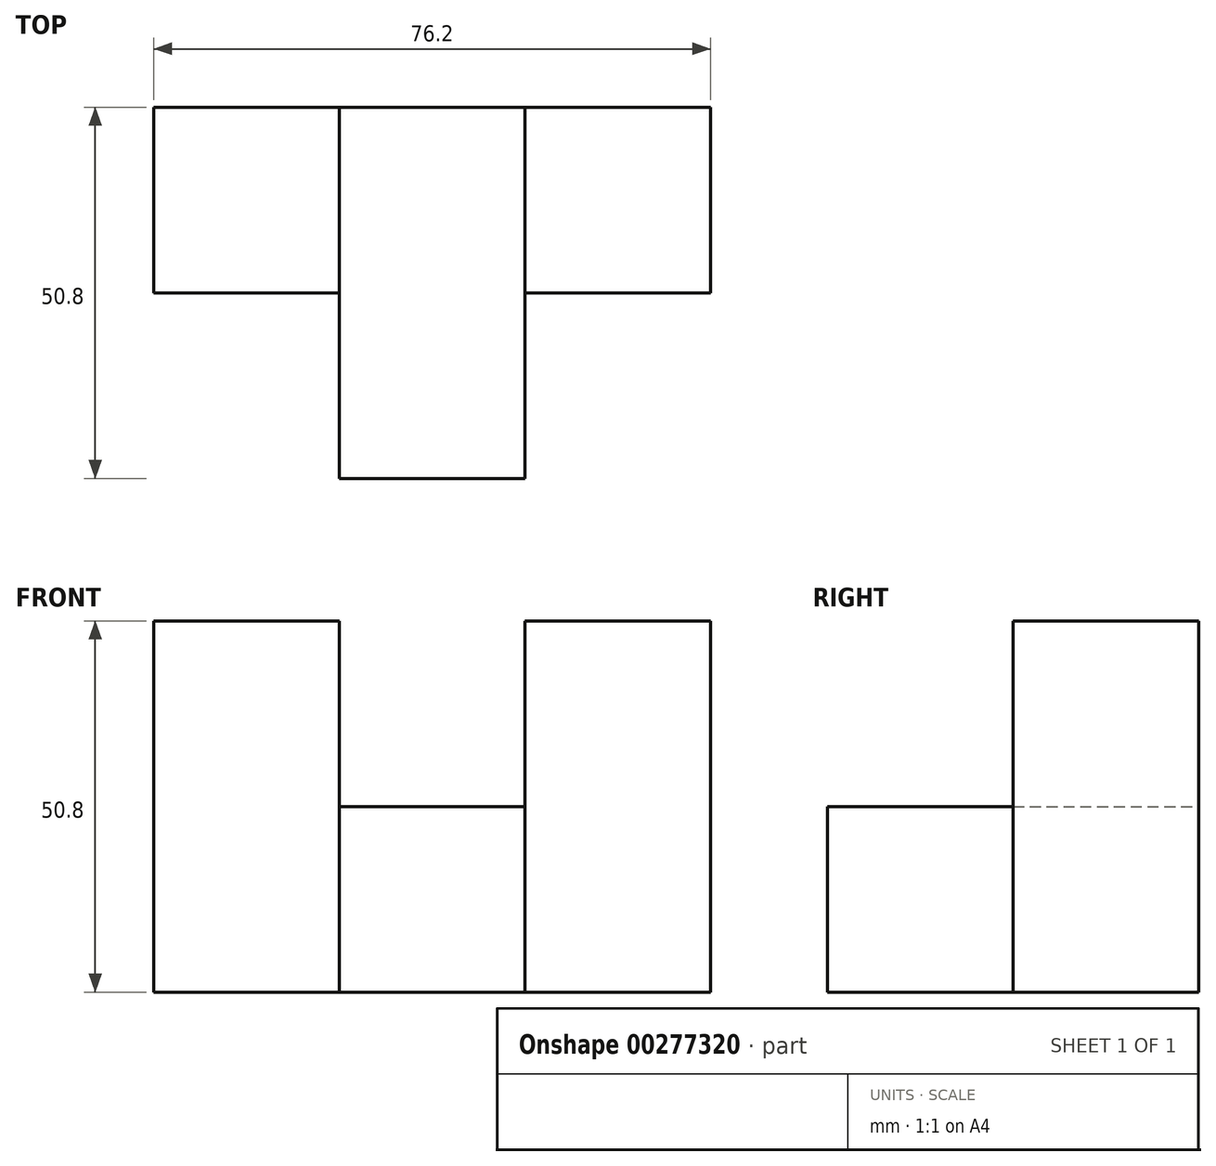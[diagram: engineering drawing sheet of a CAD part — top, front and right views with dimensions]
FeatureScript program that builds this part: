
annotation { "Feature Type Name" : "Feature", "Feature Type Description" : "" }
export const myFeature = defineFeature(function(context is Context, id is Id, definition is map)
    precondition{}
    {
        {
            var Q0;
            Q0=qCreatedBy(makeId("Front.planeOp"),FACE);
            var sketch = newSketch(context, id + "F0", { "sketchPlane" : qUnion([Q0])});
            skLineSegment(sketch, "E0", {"start": v(-59.55, -22.11) * mm, "end": v(-34.15, -22.11) * mm});
            skLineSegment(sketch, "E1", {"start": v(-34.15, -22.11) * mm, "end": v(-8.75, -22.11) * mm});
            skLineSegment(sketch, "E2", {"start": v(-8.75, -22.11) * mm, "end": v(16.65, -22.11) * mm});
            skLineSegment(sketch, "E3", {"start": v(16.65, -22.11) * mm, "end": v(16.65, 3.29) * mm});
            skLineSegment(sketch, "E4", {"start": v(16.65, 3.29) * mm, "end": v(-8.75, 3.29) * mm});
            skLineSegment(sketch, "E5", {"start": v(-8.75, 3.29) * mm, "end": v(-34.15, 3.29) * mm});
            skLineSegment(sketch, "E6", {"start": v(-34.15, 3.29) * mm, "end": v(-59.55, 3.29) * mm});
            skLineSegment(sketch, "E7", {"start": v(-59.55, 3.29) * mm, "end": v(-59.55, -22.11) * mm});
            skLineSegment(sketch, "E8", {"start": v(-34.15, 3.29) * mm, "end": v(-34.15, -22.11) * mm});
            skLineSegment(sketch, "E9", {"start": v(-8.75, 3.29) * mm, "end": v(-8.75, -22.11) * mm});
            skLineSegment(sketch, "E10", {"start": v(-59.55, 3.29) * mm, "end": v(-59.55, 28.69) * mm});
            skLineSegment(sketch, "E11", {"start": v(-59.55, 28.69) * mm, "end": v(-34.15, 28.69) * mm});
            skLineSegment(sketch, "E12", {"start": v(-34.15, 28.69) * mm, "end": v(-34.15, 3.29) * mm});
            skLineSegment(sketch, "E13", {"start": v(-8.75, 3.29) * mm, "end": v(-8.75, 28.69) * mm});
            skLineSegment(sketch, "E14", {"start": v(-8.75, 28.69) * mm, "end": v(16.65, 28.69) * mm});
            skLineSegment(sketch, "E15", {"start": v(16.65, 28.69) * mm, "end": v(16.65, 3.29) * mm});
            skSolve(sketch);
        }
        {
            var Q0;
            Q0=makeQuery(id+"F0.imprint","IMPRINT",FACE,{"disambiguationData":[TD([[makeQuery(id+"F0.imprint","IMPRINT",EDGE,{"derivedFrom":sQuery(id+"F0.wireOp",EDGE,"E1")}),1.0]])]});
            extrude(context, id + "F1", {"entities" : qUnion([Q0]), "depth" : 50.8 * mm});
        }
        {
            var Q0;
            Q0=makeQuery(id+"F0.imprint","IMPRINT",FACE,{"disambiguationData":[TD([[makeQuery(id+"F0.imprint","IMPRINT",EDGE,{"derivedFrom":sQuery(id+"F0.wireOp",EDGE,"E6")}),-1.0]])]});
            var Q1;
            Q1=makeQuery(id+"F0.imprint","IMPRINT",FACE,{"disambiguationData":[TD([[makeQuery(id+"F0.imprint","IMPRINT",EDGE,{"derivedFrom":sQuery(id+"F0.wireOp",EDGE,"E0")}),1.0]])]});
            var Q2;
            Q2=makeQuery(id+"F0.imprint","IMPRINT",FACE,{"disambiguationData":[TD([[makeQuery(id+"F0.imprint","IMPRINT",EDGE,{"derivedFrom":sQuery(id+"F0.wireOp",EDGE,"E4")}),-1.0]])]});
            var Q3;
            Q3=makeQuery(id+"F0.imprint","IMPRINT",FACE,{"disambiguationData":[TD([[makeQuery(id+"F0.imprint","IMPRINT",EDGE,{"derivedFrom":sQuery(id+"F0.wireOp",EDGE,"E2")}),1.0]])]});
            extrude(context, id + "F2", {"entities" : qUnion([Q0, Q1, Q2, Q3]), "operationType" : NewBodyOperationType.ADD, "depth" : 25.4 * mm});
        }
    });
